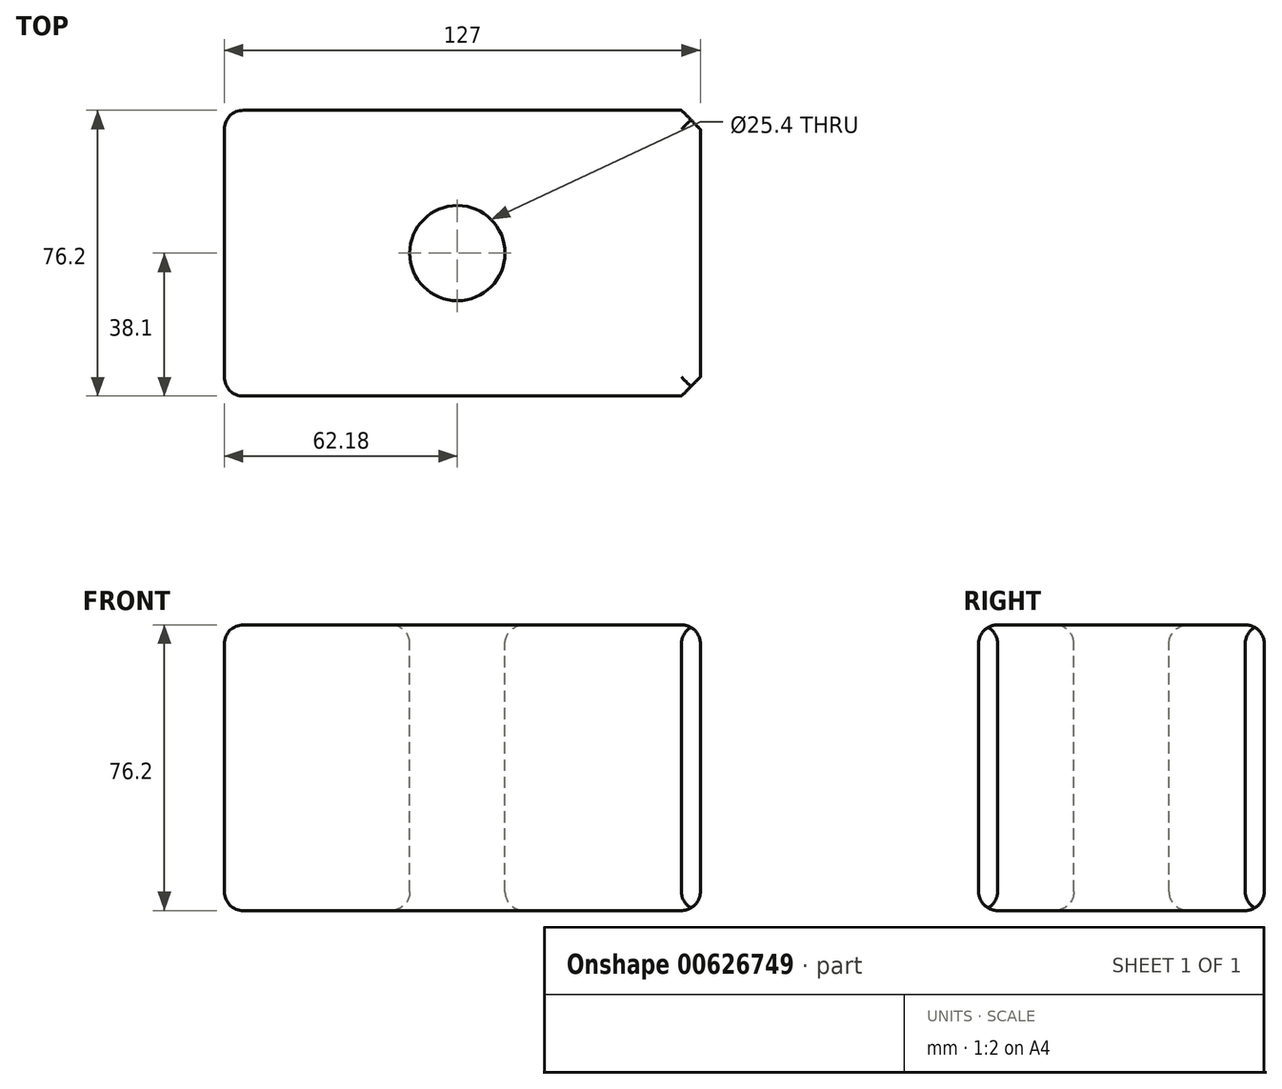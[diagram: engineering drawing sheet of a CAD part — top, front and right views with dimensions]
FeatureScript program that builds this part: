
annotation { "Feature Type Name" : "Feature", "Feature Type Description" : "" }
export const myFeature = defineFeature(function(context is Context, id is Id, definition is map)
    precondition{}
    {
        {
            var Q0;
            Q0=qCreatedBy(makeId("Front.planeOp"),FACE);
            var sketch = newSketch(context, id + "F0", { "sketchPlane" : qUnion([Q0])});
            skLineSegment(sketch, "E0", {"start": v(-62.18, 49.15) * mm, "end": v(-62.18, -27.05) * mm});
            skLineSegment(sketch, "E1", {"start": v(-62.18, -27.05) * mm, "end": v(64.82, -27.05) * mm});
            skLineSegment(sketch, "E2", {"start": v(64.82, -27.05) * mm, "end": v(64.82, 49.15) * mm});
            skLineSegment(sketch, "E3", {"start": v(64.82, 49.15) * mm, "end": v(-62.18, 49.15) * mm});
            skSolve(sketch);
        }
        {
            var Q0;
            Q0 = qSketchRegion(id + "F0", true);
            extrude(context, id + "F1", {"entities" : qUnion([Q0]), "depth" : 76.2 * mm, "offsetDistance" : 25.4 * mm});
        }
        {
            var Q0;
            Q0=makeQuery(id+"F1.opExtrude","SWEPT_FACE",FACE,{"disambiguationData":[OSD([sQuery(id+"F0.wireOp",EDGE,"E3")])]});
            var sketch = newSketch(context, id + "F2", { "sketchPlane" : qUnion([Q0])});
            skCircle(sketch, "E4", {"center": v(0, -38.1) * mm, "radius": 12.7 * mm});
            skPoint(sketch, "E4.centerSnap0", {"position": v(-62.18, -38.1) * mm});
            skSolve(sketch);
        }
        {
            var Q0;
            Q0 = qSketchRegion(id + "F2", true);
            extrude(context, id + "F3", {"entities" : qUnion([Q0]), "operationType" : NewBodyOperationType.REMOVE, "endBound" : BoundingType.THROUGH_ALL, "oppositeDirection" : true, "depth" : 25.4 * mm, "offsetDistance" : 25.4 * mm});
        }
        {
            var Q0;
            Q0=makeQuery(id+"F1.opExtrude","SWEPT_FACE",FACE,{"disambiguationData":[OSD([sQuery(id+"F0.wireOp",EDGE,"E3")])]});
            var Q1;
            Q1=makeQuery(id+"F1.opExtrude","SWEPT_FACE",FACE,{"disambiguationData":[OSD([sQuery(id+"F0.wireOp",EDGE,"E1")])]});
            fillet(context, id + "F4", {"entities" : qUnion([Q0, Q1]), "radius" : 5.08 * mm, "tangentPropagation" : true, "allowEdgeOverflow" : false});
        }
        {
            var Q0;
            Q0=makeQuery(id+"F1.opExtrude","SWEPT_FACE",FACE,{"disambiguationData":[OSD([sQuery(id+"F0.wireOp",EDGE,"E0")])]});
            fillet(context, id + "F5", {"entities" : qUnion([Q0]), "radius" : 5.08 * mm, "tangentPropagation" : true, "allowEdgeOverflow" : false});
        }
        {
            var Q0;
            Q0=makeQuery(id+"F1.opExtrude","SWEPT_FACE",FACE,{"disambiguationData":[OSD([sQuery(id+"F0.wireOp",EDGE,"E2")])]});
            chamfer(context, id + "F6", {"entities" : qUnion([Q0]), "width" : 5.08 * mm, "tangentPropagation" : true});
        }
    });
